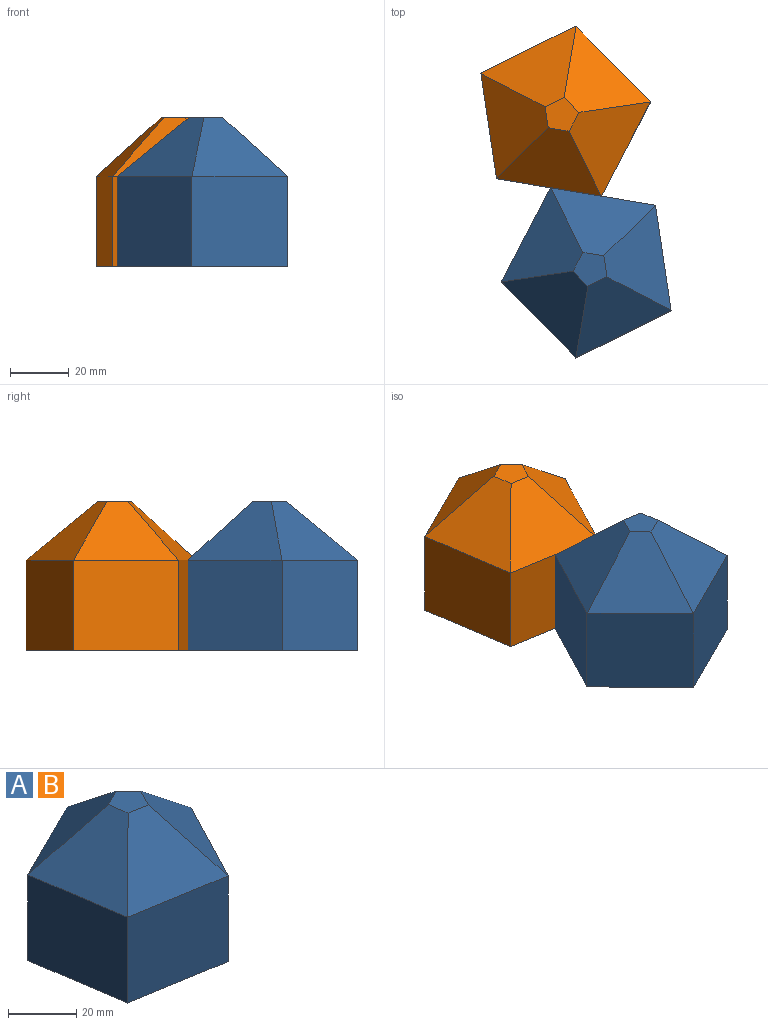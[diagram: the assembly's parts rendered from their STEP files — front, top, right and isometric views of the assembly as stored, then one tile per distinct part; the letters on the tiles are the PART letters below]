
ASSEMBLY  parts=2 mates=2
PART A: 12 faces, bbox 58x58.1x50.8 mm
  f0: plane 30.8x25.92mm, normal (0.71,0.7,0), area 1118.9mm2, adj f1,f4,f6,f11
  f1: plane 32.52x30.8mm, normal (-0.45,0.9,0), area 1118.9mm2, adj f0,f2,f6,f9
  f2: plane 35.93x30.8mm, normal (-0.99,-0.15,0), area 1118.9mm2, adj f1,f3,f6,f7
  f3: plane 35.83x30.8mm, normal (-0.17,-0.99,0), area 1118.9mm2, adj f2,f4,f6,f8
  f4: plane 32.21x30.8mm, normal (0.89,-0.46,0), area 1118.9mm2, adj f0,f3,f6,f10
  f5: plane 11.63x11.59mm, normal (0,0,1), area 90.8mm2, adj f7,f8,f9,f10,f11
  f6: plane 58.14x57.97mm, normal (0,0,-1), area 2270.4mm2, adj f0,f1,f2,f3,f4
  f7: plane 35.93x22.99mm, normal (-0.7,-0.1,0.71), area 616.5mm2, adj f2,f5,f8,f9
  f8: plane 35.83x23.33mm, normal (-0.12,-0.7,0.71), area 616.5mm2, adj f3,f5,f7,f10
  f9: plane 32.52x27.62mm, normal (-0.32,0.63,0.71), area 616.5mm2, adj f1,f5,f7,f11
  f10: plane 32.21x27.81mm, normal (0.63,-0.33,0.71), area 616.5mm2, adj f4,f5,f8,f11
  f11: plane 29.57x29.54mm, normal (0.5,0.5,0.71), area 616.5mm2, adj f0,f5,f9,f10
PART B: same geometry as A
PLACE A rot(axis=(0,0,1),108deg) t=(-45.67,-113.9,6.49)mm
PLACE B t=(-55.87,-61.49,6.49)mm
MATE planar B.f6 <-> A.f6  axis (0,0,-1) through (-60.01,-86.14,6.49)mm
MATE planar B.f3 <-> A.f4  axis (-0.17,-0.99,0) through (-60.01,-86.14,21.89)mm
